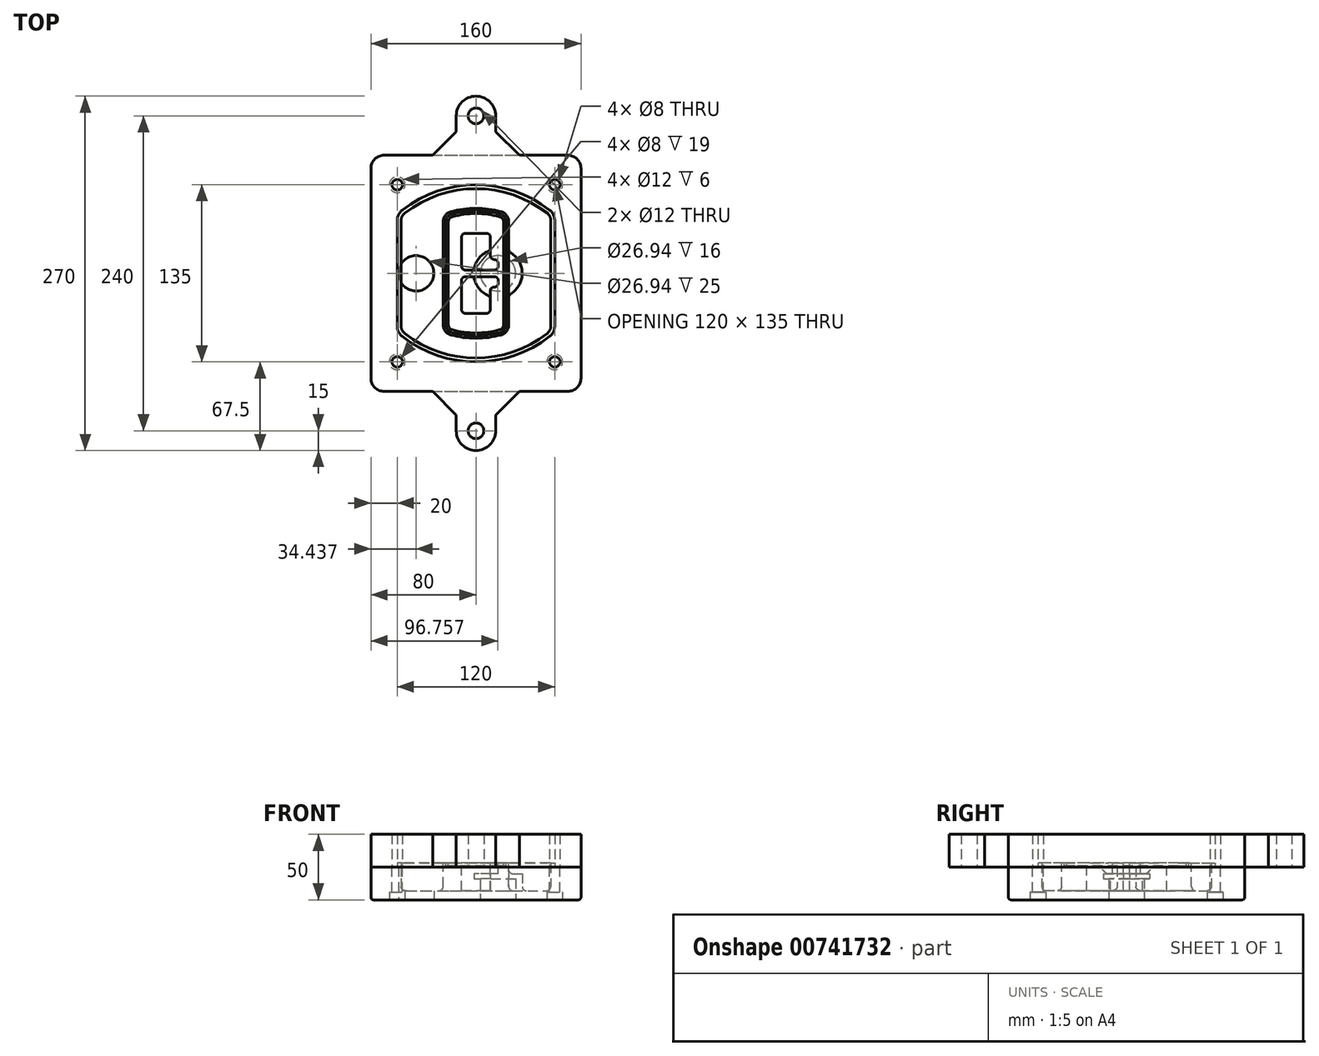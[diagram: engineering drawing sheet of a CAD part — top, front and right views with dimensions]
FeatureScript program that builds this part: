
annotation { "Feature Type Name" : "Feature", "Feature Type Description" : "" }
export const myFeature = defineFeature(function(context is Context, id is Id, definition is map)
    precondition{}
    {
        {
            var Q0;
            Q0=qCreatedBy(makeId("Top.planeOp"),FACE);
            var sketch = newSketch(context, id + "F0", { "sketchPlane" : qUnion([Q0])});
            skPoint(sketch, "E0.rect.middle", {"position": v(0, 0) * mm});
            skLineSegment(sketch, "E1.bottom", {"start": v(-70, -90) * mm, "end": v(70, -90) * mm});
            skLineSegment(sketch, "E1.top", {"start": v(-70, 90) * mm, "end": v(70, 90) * mm});
            skLineSegment(sketch, "E1.left", {"start": v(-80, -80) * mm, "end": v(-80, 80) * mm});
            skLineSegment(sketch, "E1.right", {"start": v(80, -80) * mm, "end": v(80, 80) * mm});
            skLineSegment(sketch, "E2", {"start": v(-80, 90) * mm, "end": v(80, -90) * mm, "construction": true});
            skLineSegment(sketch, "E3", {"start": v(80, 90) * mm, "end": v(-80, -90) * mm, "construction": true});
            skCircle(sketch, "E4", {"center": v(-60, 67.5) * mm, "radius": 4 * mm});
            skCircle(sketch, "E5", {"center": v(60, 67.5) * mm, "radius": 4 * mm});
            skCircle(sketch, "E6", {"center": v(60, -67.5) * mm, "radius": 4 * mm});
            skCircle(sketch, "E7", {"center": v(-60, -67.5) * mm, "radius": 4 * mm});
            skLineSegment(sketch, "E8", {"start": v(-60, 67.5) * mm, "end": v(60, 67.5) * mm, "construction": true});
            skLineSegment(sketch, "E9", {"start": v(60, 67.5) * mm, "end": v(60, -67.5) * mm, "construction": true});
            skLineSegment(sketch, "E10", {"start": v(60, -67.5) * mm, "end": v(-60, -67.5) * mm, "construction": true});
            skLineSegment(sketch, "E11", {"start": v(-60, -67.5) * mm, "end": v(-60, 67.5) * mm, "construction": true});
            skLineSegment(sketch, "E12", {"start": v(-60, 40.3) * mm, "end": v(-60, -40.3) * mm});
            skLineSegment(sketch, "E13", {"start": v(60, 40.3) * mm, "end": v(60, -40.3) * mm});
            skArc(sketch, "E14", {"start": v(56.15, 48.18) * mm, "mid": v(0, 67.5) * mm, "end": v(-56.15, 48.18) * mm});
            skArc(sketch, "E15", {"start": v(-56.15, -48.18) * mm, "mid": v(0, -67.5) * mm, "end": v(56.15, -48.18) * mm});
            skLineSegment(sketch, "E16", {"start": v(-60, 0) * mm, "end": v(60, 0) * mm, "construction": true});
            skPoint(sketch, "E17.visualSharp", {"position": v(-60, -45) * mm});
            skArc(sketch, "E17.filletArc", {"start": v(-60, -40.3) * mm, "mid": v(-58.99, -44.68) * mm, "end": v(-56.15, -48.18) * mm});
            skPoint(sketch, "E18.visualSharp", {"position": v(-60, 45) * mm});
            skArc(sketch, "E18.filletArc", {"start": v(-56.15, 48.18) * mm, "mid": v(-58.99, 44.68) * mm, "end": v(-60, 40.3) * mm});
            skPoint(sketch, "E19.visualSharp", {"position": v(60, 45) * mm});
            skArc(sketch, "E19.filletArc", {"start": v(60, 40.3) * mm, "mid": v(58.99, 44.68) * mm, "end": v(56.15, 48.18) * mm});
            skPoint(sketch, "E20.visualSharp", {"position": v(60, -45) * mm});
            skArc(sketch, "E20.filletArc", {"start": v(56.15, -48.18) * mm, "mid": v(58.99, -44.68) * mm, "end": v(60, -40.3) * mm});
            skPoint(sketch, "E21.visualSharp", {"position": v(-80, 90) * mm});
            skArc(sketch, "E21.filletArc", {"start": v(-70, 90) * mm, "mid": v(-77.07, 87.07) * mm, "end": v(-80, 80) * mm});
            skPoint(sketch, "E22.visualSharp", {"position": v(80, 90) * mm});
            skArc(sketch, "E22.filletArc", {"start": v(80, 80) * mm, "mid": v(77.07, 87.07) * mm, "end": v(70, 90) * mm});
            skPoint(sketch, "E23.visualSharp", {"position": v(80, -90) * mm});
            skArc(sketch, "E23.filletArc", {"start": v(70, -90) * mm, "mid": v(77.07, -87.07) * mm, "end": v(80, -80) * mm});
            skPoint(sketch, "E24.visualSharp", {"position": v(-80, -90) * mm});
            skArc(sketch, "E24.filletArc", {"start": v(-80, -80) * mm, "mid": v(-77.07, -87.07) * mm, "end": v(-70, -90) * mm});
            skArc(sketch, "E25.0", {"start": v(57, 40.3) * mm, "mid": v(56.3, 43.36) * mm, "end": v(54.3, 45.81) * mm});
            skLineSegment(sketch, "E25.1", {"start": v(57, 40.3) * mm, "end": v(57, -40.3) * mm});
            skArc(sketch, "E25.2", {"start": v(54.3, -45.81) * mm, "mid": v(56.3, -43.36) * mm, "end": v(57, -40.3) * mm});
            skArc(sketch, "E25.3", {"start": v(-54.3, -45.81) * mm, "mid": v(0, -64.5) * mm, "end": v(54.3, -45.81) * mm});
            skArc(sketch, "E25.4", {"start": v(-57, -40.3) * mm, "mid": v(-56.3, -43.36) * mm, "end": v(-54.3, -45.81) * mm});
            skArc(sketch, "E25.5", {"start": v(54.3, 45.81) * mm, "mid": v(0, 64.5) * mm, "end": v(-54.3, 45.81) * mm});
            skLineSegment(sketch, "E25.6", {"start": v(-57, 40.3) * mm, "end": v(-57, -40.3) * mm});
            skArc(sketch, "E25.7", {"start": v(-54.3, 45.81) * mm, "mid": v(-56.3, 43.36) * mm, "end": v(-57, 40.3) * mm});
            skArc(sketch, "E26.0", {"start": v(-58.62, 51.33) * mm, "mid": v(-62.58, 46.43) * mm, "end": v(-64, 40.3) * mm});
            skArc(sketch, "E26.1", {"start": v(58.62, 51.33) * mm, "mid": v(0, 71.5) * mm, "end": v(-58.62, 51.33) * mm});
            skArc(sketch, "E26.2", {"start": v(64, 40.3) * mm, "mid": v(62.58, 46.43) * mm, "end": v(58.62, 51.33) * mm});
            skLineSegment(sketch, "E26.3", {"start": v(64, 40.3) * mm, "end": v(64, -40.3) * mm});
            skArc(sketch, "E26.4", {"start": v(58.62, -51.33) * mm, "mid": v(62.58, -46.43) * mm, "end": v(64, -40.3) * mm});
            skLineSegment(sketch, "E26.5", {"start": v(-64, 40.3) * mm, "end": v(-64, -40.3) * mm});
            skArc(sketch, "E26.6", {"start": v(-58.62, -51.33) * mm, "mid": v(0, -71.5) * mm, "end": v(58.62, -51.33) * mm});
            skArc(sketch, "E26.7", {"start": v(-64, -40.3) * mm, "mid": v(-62.58, -46.43) * mm, "end": v(-58.62, -51.33) * mm});
            skSolve(sketch);
        }
        {
            var Q0;
            Q0=makeQuery(id+"F0.imprint","IMPRINT",FACE,{"disambiguationData":[TD([[makeQuery(id+"F0.imprint","IMPRINT",EDGE,{"derivedFrom":sQuery(id+"F0.wireOp",EDGE,"E1.bottom")}),1.0]])]});
            var Q1;
            Q1=makeQuery(id+"F0.imprint","IMPRINT",FACE,{"disambiguationData":[TD([[makeQuery(id+"F0.imprint","IMPRINT",EDGE,{"derivedFrom":sQuery(id+"F0.wireOp",EDGE,"E12")}),1.0]])]});
            var Q2;
            Q2=makeQuery(id+"F0.imprint","IMPRINT",FACE,{"disambiguationData":[TD([[makeQuery(id+"F0.imprint","IMPRINT",EDGE,{"derivedFrom":sQuery(id+"F0.wireOp",EDGE,"E25.0")}),1.0]])]});
            var Q3;
            Q3=makeQuery(id+"F0.imprint","IMPRINT",FACE,{"disambiguationData":[TD([[makeQuery(id+"F0.imprint","IMPRINT",EDGE,{"derivedFrom":sQuery(id+"F0.wireOp",EDGE,"E12")}),-1.0]])]});
            extrude(context, id + "F1", {"entities" : qUnion([Q0, Q1, Q2, Q3]), "oppositeDirection" : true, "depth" : 25 * mm});
        }
        {
            var Q0;
            Q0=makeQuery(id+"F0.imprint","IMPRINT",FACE,{"disambiguationData":[TD([[makeQuery(id+"F0.imprint","IMPRINT",EDGE,{"derivedFrom":sQuery(id+"F0.wireOp",EDGE,"E12")}),1.0]])]});
            extrude(context, id + "F2", {"entities" : qUnion([Q0]), "operationType" : NewBodyOperationType.ADD, "depth" : 3 * mm});
        }
        {
            var Q0;
            Q0=makeQuery(id+"F0.imprint","IMPRINT",FACE,{"disambiguationData":[TD([[makeQuery(id+"F0.imprint","IMPRINT",EDGE,{"derivedFrom":sQuery(id+"F0.wireOp",EDGE,"E25.0")}),1.0]])]});
            extrude(context, id + "F3", {"entities" : qUnion([Q0]), "operationType" : NewBodyOperationType.REMOVE, "oppositeDirection" : true, "depth" : 18 * mm});
        }
        {
            var Q0;
            Q0=makeQuery(id+"F2.opExtrude","CAP_FACE",FACE,{"disambiguationData":[OSD([sQuery(id+"F0.wireOp",EDGE,"E12"),sQuery(id+"F0.wireOp",EDGE,"E13"),sQuery(id+"F0.wireOp",EDGE,"E14"),sQuery(id+"F0.wireOp",EDGE,"E15"),sQuery(id+"F0.wireOp",EDGE,"E17.filletArc"),sQuery(id+"F0.wireOp",EDGE,"E18.filletArc"),sQuery(id+"F0.wireOp",EDGE,"E19.filletArc"),sQuery(id+"F0.wireOp",EDGE,"E20.filletArc"),sQuery(id+"F0.wireOp",EDGE,"E25.0"),sQuery(id+"F0.wireOp",EDGE,"E25.1"),sQuery(id+"F0.wireOp",EDGE,"E25.2"),sQuery(id+"F0.wireOp",EDGE,"E25.3"),sQuery(id+"F0.wireOp",EDGE,"E25.4"),sQuery(id+"F0.wireOp",EDGE,"E25.5"),sQuery(id+"F0.wireOp",EDGE,"E25.6"),sQuery(id+"F0.wireOp",EDGE,"E25.7")])],"isStart":false});
            var sketch = newSketch(context, id + "F4", { "sketchPlane" : qUnion([Q0])});
            skArc(sketch, "E27.0", {"start": v(-19.08, -46.97) * mm, "mid": v(0, -49.5) * mm, "end": v(19.08, -46.97) * mm});
            skArc(sketch, "E28.0", {"start": v(19.08, 46.97) * mm, "mid": v(0, 49.5) * mm, "end": v(-19.08, 46.97) * mm});
            skLineSegment(sketch, "E29", {"start": v(-25, 39.25) * mm, "end": v(-25, -39.25) * mm});
            skLineSegment(sketch, "E30", {"start": v(25, 39.25) * mm, "end": v(25, -39.25) * mm});
            skLineSegment(sketch, "E31", {"start": v(-25, 45.1) * mm, "end": v(25, 45.1) * mm, "construction": true});
            skLineSegment(sketch, "E32", {"start": v(-25, -45.1) * mm, "end": v(25, -45.1) * mm, "construction": true});
            skPoint(sketch, "E33.visualSharp", {"position": v(-25, 45.1) * mm});
            skArc(sketch, "E33.filletArc", {"start": v(-19.08, 46.97) * mm, "mid": v(-23.35, 44.11) * mm, "end": v(-25, 39.25) * mm});
            skPoint(sketch, "E34.visualSharp", {"position": v(25, 45.1) * mm});
            skArc(sketch, "E34.filletArc", {"start": v(25, 39.25) * mm, "mid": v(23.35, 44.11) * mm, "end": v(19.08, 46.97) * mm});
            skPoint(sketch, "E35.visualSharp", {"position": v(25, -45.1) * mm});
            skArc(sketch, "E35.filletArc", {"start": v(19.08, -46.97) * mm, "mid": v(23.35, -44.11) * mm, "end": v(25, -39.25) * mm});
            skPoint(sketch, "E36.visualSharp", {"position": v(-25, -45.1) * mm});
            skArc(sketch, "E36.filletArc", {"start": v(-25, -39.25) * mm, "mid": v(-23.35, -44.11) * mm, "end": v(-19.08, -46.97) * mm});
            skArc(sketch, "E37.0", {"start": v(54.3, 45.81) * mm, "mid": v(0, 64.5) * mm, "end": v(-54.3, 45.81) * mm});
            skArc(sketch, "E37.1", {"start": v(-54.3, 45.81) * mm, "mid": v(-56.3, 43.36) * mm, "end": v(-57, 40.3) * mm});
            skLineSegment(sketch, "E37.2", {"start": v(-57, 40.3) * mm, "end": v(-57, -40.3) * mm});
            skArc(sketch, "E37.3", {"start": v(-57, -40.3) * mm, "mid": v(-56.3, -43.36) * mm, "end": v(-54.3, -45.81) * mm});
            skArc(sketch, "E37.4", {"start": v(-54.3, -45.81) * mm, "mid": v(0, -64.5) * mm, "end": v(54.3, -45.81) * mm});
            skArc(sketch, "E37.5", {"start": v(54.3, -45.81) * mm, "mid": v(56.3, -43.36) * mm, "end": v(57, -40.3) * mm});
            skLineSegment(sketch, "E37.6", {"start": v(57, 40.3) * mm, "end": v(57, -40.3) * mm});
            skArc(sketch, "E37.7", {"start": v(57, 40.3) * mm, "mid": v(56.3, 43.36) * mm, "end": v(54.3, 45.81) * mm});
            skLineSegment(sketch, "E38.0", {"start": v(23, 39.25) * mm, "end": v(23, -39.25) * mm});
            skArc(sketch, "E38.1", {"start": v(18.56, -45.04) * mm, "mid": v(21.76, -42.9) * mm, "end": v(23, -39.25) * mm});
            skArc(sketch, "E38.2", {"start": v(-18.56, -45.04) * mm, "mid": v(0, -47.5) * mm, "end": v(18.56, -45.04) * mm});
            skArc(sketch, "E38.3", {"start": v(-23, -39.25) * mm, "mid": v(-21.76, -42.9) * mm, "end": v(-18.56, -45.04) * mm});
            skLineSegment(sketch, "E38.4", {"start": v(-23, 39.25) * mm, "end": v(-23, -39.25) * mm});
            skArc(sketch, "E38.5", {"start": v(23, 39.25) * mm, "mid": v(21.76, 42.9) * mm, "end": v(18.56, 45.04) * mm});
            skArc(sketch, "E38.6", {"start": v(-18.56, 45.04) * mm, "mid": v(-21.76, 42.9) * mm, "end": v(-23, 39.25) * mm});
            skArc(sketch, "E38.7", {"start": v(18.56, 45.04) * mm, "mid": v(0, 47.5) * mm, "end": v(-18.56, 45.04) * mm});
            skArc(sketch, "E39.0", {"start": v(21, 39.25) * mm, "mid": v(20.18, 41.68) * mm, "end": v(18.04, 43.1) * mm});
            skLineSegment(sketch, "E39.1", {"start": v(21, 39.25) * mm, "end": v(21, -39.25) * mm});
            skArc(sketch, "E39.2", {"start": v(18.04, -43.1) * mm, "mid": v(20.18, -41.68) * mm, "end": v(21, -39.25) * mm});
            skArc(sketch, "E39.3", {"start": v(-18.04, -43.1) * mm, "mid": v(0, -45.5) * mm, "end": v(18.04, -43.1) * mm});
            skArc(sketch, "E39.4", {"start": v(-21, -39.25) * mm, "mid": v(-20.18, -41.68) * mm, "end": v(-18.04, -43.1) * mm});
            skArc(sketch, "E39.5", {"start": v(18.04, 43.1) * mm, "mid": v(0, 45.5) * mm, "end": v(-18.04, 43.1) * mm});
            skLineSegment(sketch, "E39.6", {"start": v(-21, 39.25) * mm, "end": v(-21, -39.25) * mm});
            skArc(sketch, "E39.7", {"start": v(-18.04, 43.1) * mm, "mid": v(-20.18, 41.68) * mm, "end": v(-21, 39.25) * mm});
            skLineSegment(sketch, "E40", {"start": v(-25, 0) * mm, "end": v(25, 0) * mm, "construction": true});
            skLineSegment(sketch, "E41", {"start": v(-11, 5.5) * mm, "end": v(-11, 27.5) * mm});
            skLineSegment(sketch, "E42", {"start": v(-8, 30.5) * mm, "end": v(8, 30.5) * mm});
            skLineSegment(sketch, "E43", {"start": v(11, 27.5) * mm, "end": v(11, 13.5) * mm});
            skLineSegment(sketch, "E44", {"start": v(14, 10.5) * mm, "end": v(14, 10.5) * mm});
            skLineSegment(sketch, "E45", {"start": v(17, 7.5) * mm, "end": v(17, 5.5) * mm});
            skLineSegment(sketch, "E46", {"start": v(14, 2.5) * mm, "end": v(-8, 2.5) * mm});
            skPoint(sketch, "E47.visualSharp", {"position": v(-11, 30.5) * mm});
            skArc(sketch, "E47.filletArc", {"start": v(-8, 30.5) * mm, "mid": v(-10.12, 29.62) * mm, "end": v(-11, 27.5) * mm});
            skPoint(sketch, "E48.visualSharp", {"position": v(11, 30.5) * mm});
            skArc(sketch, "E48.filletArc", {"start": v(11, 27.5) * mm, "mid": v(10.12, 29.62) * mm, "end": v(8, 30.5) * mm});
            skPoint(sketch, "E49.visualSharp", {"position": v(11, 10.5) * mm});
            skArc(sketch, "E49.filletArc", {"start": v(11, 13.5) * mm, "mid": v(11.88, 11.38) * mm, "end": v(14, 10.5) * mm});
            skPoint(sketch, "E50.visualSharp", {"position": v(17, 10.5) * mm});
            skArc(sketch, "E50.filletArc", {"start": v(17, 7.5) * mm, "mid": v(16.12, 9.62) * mm, "end": v(14, 10.5) * mm});
            skPoint(sketch, "E51.visualSharp", {"position": v(17, 2.5) * mm});
            skArc(sketch, "E51.filletArc", {"start": v(14, 2.5) * mm, "mid": v(16.12, 3.38) * mm, "end": v(17, 5.5) * mm});
            skPoint(sketch, "E52.visualSharp", {"position": v(-11, 2.5) * mm});
            skArc(sketch, "E52.filletArc", {"start": v(-11, 5.5) * mm, "mid": v(-10.12, 3.38) * mm, "end": v(-8, 2.5) * mm});
            skLineSegment(sketch, "E53.0.MirrorCS", {"start": v(14, -2.5) * mm, "end": v(-8, -2.5) * mm});
            skArc(sketch, "E54.0.MirrorCS", {"start": v(-11, -5.5) * mm, "mid": v(-10.12, -3.38) * mm, "end": v(-8, -2.5) * mm});
            skLineSegment(sketch, "E55.0.MirrorCS", {"start": v(-11, -5.5) * mm, "end": v(-11, -27.5) * mm});
            skArc(sketch, "E56.0.MirrorCS", {"start": v(-8, -30.5) * mm, "mid": v(-10.12, -29.62) * mm, "end": v(-11, -27.5) * mm});
            skLineSegment(sketch, "E57.0.MirrorCS", {"start": v(-8, -30.5) * mm, "end": v(8, -30.5) * mm});
            skArc(sketch, "E58.0.MirrorCS", {"start": v(11, -27.5) * mm, "mid": v(10.12, -29.62) * mm, "end": v(8, -30.5) * mm});
            skLineSegment(sketch, "E59.0.MirrorCS", {"start": v(11, -27.5) * mm, "end": v(11, -13.5) * mm});
            skArc(sketch, "E60.0.MirrorCS", {"start": v(11, -13.5) * mm, "mid": v(11.88, -11.38) * mm, "end": v(14, -10.5) * mm});
            skArc(sketch, "E61.0.MirrorCS", {"start": v(17, -7.5) * mm, "mid": v(16.12, -9.62) * mm, "end": v(14, -10.5) * mm});
            skLineSegment(sketch, "E62.0.MirrorCS", {"start": v(17, -7.5) * mm, "end": v(17, -5.5) * mm});
            skArc(sketch, "E63.0.MirrorCS", {"start": v(14, -2.5) * mm, "mid": v(16.12, -3.38) * mm, "end": v(17, -5.5) * mm});
            skSolve(sketch);
        }
        {
            var Q0;
            Q0=makeQuery(id+"F4.imprint","IMPRINT",FACE,{"disambiguationData":[TD([[makeQuery(id+"F4.imprint","IMPRINT",EDGE,{"derivedFrom":sQuery(id+"F4.wireOp",EDGE,"E27.0")}),1.0]])]});
            var Q1;
            Q1=makeQuery(id+"F4.imprint","IMPRINT",FACE,{"disambiguationData":[TD([[makeQuery(id+"F4.imprint","IMPRINT",EDGE,{"derivedFrom":sQuery(id+"F4.wireOp",EDGE,"E38.0")}),-1.0]])]});
            var Q2;
            Q2=makeQuery(id+"F4.imprint","IMPRINT",FACE,{"disambiguationData":[TD([[makeQuery(id+"F4.imprint","IMPRINT",EDGE,{"derivedFrom":sQuery(id+"F4.wireOp",EDGE,"E39.0")}),1.0]])]});
            extrude(context, id + "F5", {"entities" : qUnion([Q0, Q1, Q2]), "operationType" : NewBodyOperationType.ADD, "endBound" : BoundingType.UP_TO_NEXT, "oppositeDirection" : true, "depth" : 25 * mm});
        }
        {
            var Q0;
            Q0=makeQuery(id+"F4.imprint","IMPRINT",FACE,{"disambiguationData":[TD([[makeQuery(id+"F4.imprint","IMPRINT",EDGE,{"derivedFrom":sQuery(id+"F4.wireOp",EDGE,"E38.0")}),-1.0]])]});
            extrude(context, id + "F6", {"entities" : qUnion([Q0]), "operationType" : NewBodyOperationType.REMOVE, "oppositeDirection" : true, "depth" : 2 * mm});
        }
        {
            var Q0;
            Q0=makeQuery(id+"F1.opExtrude","CAP_FACE",FACE,{"disambiguationData":[OSD([sQuery(id+"F0.wireOp",EDGE,"E1.bottom"),sQuery(id+"F0.wireOp",EDGE,"E1.top"),sQuery(id+"F0.wireOp",EDGE,"E1.left"),sQuery(id+"F0.wireOp",EDGE,"E1.right"),sQuery(id+"F0.wireOp",EDGE,"E4"),sQuery(id+"F0.wireOp",EDGE,"E5"),sQuery(id+"F0.wireOp",EDGE,"E6"),sQuery(id+"F0.wireOp",EDGE,"E7"),sQuery(id+"F0.wireOp",EDGE,"E21.filletArc"),sQuery(id+"F0.wireOp",EDGE,"E22.filletArc"),sQuery(id+"F0.wireOp",EDGE,"E23.filletArc"),sQuery(id+"F0.wireOp",EDGE,"E24.filletArc")])],"isStart":false});
            var sketch = newSketch(context, id + "F7", { "sketchPlane" : qUnion([Q0])});
            skCircle(sketch, "E64", {"center": v(16.76, 0) * mm, "radius": 13.47 * mm});
            skCircle(sketch, "E65", {"center": v(-45.56, 0) * mm, "radius": 13.47 * mm});
            skLineSegment(sketch, "E66", {"start": v(80, 0) * mm, "end": v(-80, 0) * mm});
            skCircle(sketch, "E67", {"center": v(16.76, 0) * mm, "radius": 18.47 * mm});
            skCircle(sketch, "E68", {"center": v(60, -67.5) * mm, "radius": 6 * mm});
            skCircle(sketch, "E69", {"center": v(-60, -67.5) * mm, "radius": 6 * mm});
            skCircle(sketch, "E70", {"center": v(-60, 67.5) * mm, "radius": 6 * mm});
            skCircle(sketch, "E71", {"center": v(60, 67.5) * mm, "radius": 6 * mm});
            skSolve(sketch);
        }
        {
            var Q0;
            {var subQ1=sQuery(id+"F7.wireOp",EDGE,"E66");var subQ4=sQuery(id+"F7.wireOp",EDGE,"E64");var subQ6=makeQuery(id+"F7.imprint","INTERSECT",VERTEX,{"disambiguationData":[OD(0.0)],"derivedFrom":[subQ4,subQ1]});Q0=makeQuery(id+"F7.imprint","IMPRINT",FACE,{"disambiguationData":[TD([[makeQuery(id+"F7.imprint","IMPRINT",EDGE,{"disambiguationData":[TD([[subQ6,-1.0]])],"derivedFrom":subQ4}),-1.0]])]});}
            var Q1;
            {var subQ0=sQuery(id+"F7.wireOp",EDGE,"E66");var subQ1=sQuery(id+"F7.wireOp",EDGE,"E64");var subQ3=makeQuery(id+"F7.imprint","INTERSECT",VERTEX,{"disambiguationData":[OD(0.0)],"derivedFrom":[subQ1,subQ0]});Q1=makeQuery(id+"F7.imprint","IMPRINT",FACE,{"disambiguationData":[TD([[makeQuery(id+"F7.imprint","IMPRINT",EDGE,{"disambiguationData":[TD([[subQ3,-1.0]])],"derivedFrom":subQ1}),1.0]])]});}
            var Q2;
            {var subQ0=sQuery(id+"F7.wireOp",EDGE,"E66");var subQ1=sQuery(id+"F7.wireOp",EDGE,"E64");var subQ3=makeQuery(id+"F7.imprint","INTERSECT",VERTEX,{"disambiguationData":[OD(0.0)],"derivedFrom":[subQ1,subQ0]});Q2=makeQuery(id+"F7.imprint","IMPRINT",FACE,{"disambiguationData":[TD([[makeQuery(id+"F7.imprint","IMPRINT",EDGE,{"disambiguationData":[TD([[subQ3,1.0]])],"derivedFrom":subQ1}),1.0]])]});}
            var Q3;
            {var subQ1=sQuery(id+"F7.wireOp",EDGE,"E66");var subQ4=sQuery(id+"F7.wireOp",EDGE,"E64");var subQ6=makeQuery(id+"F7.imprint","INTERSECT",VERTEX,{"disambiguationData":[OD(0.0)],"derivedFrom":[subQ4,subQ1]});Q3=makeQuery(id+"F7.imprint","IMPRINT",FACE,{"disambiguationData":[TD([[makeQuery(id+"F7.imprint","IMPRINT",EDGE,{"disambiguationData":[TD([[subQ6,1.0]])],"derivedFrom":subQ4}),-1.0]])]});}
            extrude(context, id + "F8", {"entities" : qUnion([Q0, Q1, Q2, Q3]), "operationType" : NewBodyOperationType.ADD, "oppositeDirection" : true, "depth" : 20 * mm});
        }
        {
            var Q0;
            {var subQ0=sQuery(id+"F7.wireOp",EDGE,"E66");var subQ1=sQuery(id+"F7.wireOp",EDGE,"E64");var subQ3=makeQuery(id+"F7.imprint","INTERSECT",VERTEX,{"disambiguationData":[OD(0.0)],"derivedFrom":[subQ1,subQ0]});Q0=makeQuery(id+"F7.imprint","IMPRINT",FACE,{"disambiguationData":[TD([[makeQuery(id+"F7.imprint","IMPRINT",EDGE,{"disambiguationData":[TD([[subQ3,-1.0]])],"derivedFrom":subQ1}),1.0]])]});}
            var Q1;
            {var subQ0=sQuery(id+"F7.wireOp",EDGE,"E66");var subQ1=sQuery(id+"F7.wireOp",EDGE,"E64");var subQ3=makeQuery(id+"F7.imprint","INTERSECT",VERTEX,{"disambiguationData":[OD(0.0)],"derivedFrom":[subQ1,subQ0]});Q1=makeQuery(id+"F7.imprint","IMPRINT",FACE,{"disambiguationData":[TD([[makeQuery(id+"F7.imprint","IMPRINT",EDGE,{"disambiguationData":[TD([[subQ3,1.0]])],"derivedFrom":subQ1}),1.0]])]});}
            extrude(context, id + "F9", {"entities" : qUnion([Q0, Q1]), "operationType" : NewBodyOperationType.REMOVE, "oppositeDirection" : true, "depth" : 16 * mm});
        }
        {
            var Q0;
            {var subQ0=sQuery(id+"F7.wireOp",EDGE,"E66");var subQ1=sQuery(id+"F7.wireOp",EDGE,"E65");var subQ3=makeQuery(id+"F7.imprint","INTERSECT",VERTEX,{"disambiguationData":[OD(0.0)],"derivedFrom":[subQ1,subQ0]});Q0=makeQuery(id+"F7.imprint","IMPRINT",FACE,{"disambiguationData":[TD([[makeQuery(id+"F7.imprint","IMPRINT",EDGE,{"disambiguationData":[TD([[subQ3,-1.0]])],"derivedFrom":subQ1}),1.0]])]});}
            var Q1;
            {var subQ0=sQuery(id+"F7.wireOp",EDGE,"E66");var subQ1=sQuery(id+"F7.wireOp",EDGE,"E65");var subQ3=makeQuery(id+"F7.imprint","INTERSECT",VERTEX,{"disambiguationData":[OD(0.0)],"derivedFrom":[subQ1,subQ0]});Q1=makeQuery(id+"F7.imprint","IMPRINT",FACE,{"disambiguationData":[TD([[makeQuery(id+"F7.imprint","IMPRINT",EDGE,{"disambiguationData":[TD([[subQ3,1.0]])],"derivedFrom":subQ1}),1.0]])]});}
            extrude(context, id + "F10", {"entities" : qUnion([Q0, Q1]), "operationType" : NewBodyOperationType.REMOVE, "oppositeDirection" : true, "depth" : 25 * mm});
        }
        {
            var Q0;
            Q0=makeQuery(id+"F7.imprint","IMPRINT",FACE,{"disambiguationData":[TD([[makeQuery(id+"F7.imprint","IMPRINT",EDGE,{"derivedFrom":sQuery(id+"F7.wireOp",EDGE,"E68")}),1.0]])]});
            var Q1;
            Q1=makeQuery(id+"F7.imprint","IMPRINT",FACE,{"disambiguationData":[TD([[makeQuery(id+"F7.imprint","IMPRINT",EDGE,{"derivedFrom":makeQuery(id+"F1.opExtrude","CAP_EDGE",EDGE,{"disambiguationData":[OSD([sQuery(id+"F0.wireOp",EDGE,"E5")])],"isStart":false})}),-1.0]])]});
            var Q2;
            Q2=makeQuery(id+"F7.imprint","IMPRINT",FACE,{"disambiguationData":[TD([[makeQuery(id+"F7.imprint","IMPRINT",EDGE,{"derivedFrom":sQuery(id+"F7.wireOp",EDGE,"E69")}),1.0]])]});
            var Q3;
            Q3=makeQuery(id+"F7.imprint","IMPRINT",FACE,{"disambiguationData":[TD([[makeQuery(id+"F7.imprint","IMPRINT",EDGE,{"derivedFrom":makeQuery(id+"F1.opExtrude","CAP_EDGE",EDGE,{"disambiguationData":[OSD([sQuery(id+"F0.wireOp",EDGE,"E4")])],"isStart":false})}),-1.0]])]});
            var Q4;
            Q4=makeQuery(id+"F7.imprint","IMPRINT",FACE,{"disambiguationData":[TD([[makeQuery(id+"F7.imprint","IMPRINT",EDGE,{"derivedFrom":sQuery(id+"F7.wireOp",EDGE,"E70")}),1.0]])]});
            var Q5;
            Q5=makeQuery(id+"F7.imprint","IMPRINT",FACE,{"disambiguationData":[TD([[makeQuery(id+"F7.imprint","IMPRINT",EDGE,{"derivedFrom":makeQuery(id+"F1.opExtrude","CAP_EDGE",EDGE,{"disambiguationData":[OSD([sQuery(id+"F0.wireOp",EDGE,"E7")])],"isStart":false})}),-1.0]])]});
            var Q6;
            Q6=makeQuery(id+"F7.imprint","IMPRINT",FACE,{"disambiguationData":[TD([[makeQuery(id+"F7.imprint","IMPRINT",EDGE,{"derivedFrom":sQuery(id+"F7.wireOp",EDGE,"E71")}),1.0]])]});
            var Q7;
            Q7=makeQuery(id+"F7.imprint","IMPRINT",FACE,{"disambiguationData":[TD([[makeQuery(id+"F7.imprint","IMPRINT",EDGE,{"derivedFrom":makeQuery(id+"F1.opExtrude","CAP_EDGE",EDGE,{"disambiguationData":[OSD([sQuery(id+"F0.wireOp",EDGE,"E6")])],"isStart":false})}),-1.0]])]});
            extrude(context, id + "F11", {"entities" : qUnion([Q0, Q1, Q2, Q3, Q4, Q5, Q6, Q7]), "operationType" : NewBodyOperationType.REMOVE, "oppositeDirection" : true, "depth" : 6 * mm});
        }
        {
            var Q0;
            Q0=makeQuery(id+"F9.boolean.opBoolean","COPY",FACE,{"derivedFrom":makeQuery(id+"F9.opExtrude","CAP_FACE",FACE,{"disambiguationData":[OSD([sQuery(id+"F7.wireOp",EDGE,"E64")])],"isStart":false})});
            var sketch = newSketch(context, id + "F12", { "sketchPlane" : qUnion([Q0])});
            skArc(sketch, "E72.0", {"start": v(11, 17.55) * mm, "mid": v(2.57, 11.82) * mm, "end": v(-1.54, 2.5) * mm});
            skArc(sketch, "E72.1", {"start": v(-1.54, -2.5) * mm, "mid": v(2.57, -11.82) * mm, "end": v(11, -17.55) * mm});
            skLineSegment(sketch, "E73", {"start": v(-1.54, -2.5) * mm, "end": v(14, -2.5) * mm});
            skLineSegment(sketch, "E74.0", {"start": v(14, 2.5) * mm, "end": v(-1.54, 2.5) * mm});
            skArc(sketch, "E74.1", {"start": v(14, 2.5) * mm, "mid": v(16.12, 3.38) * mm, "end": v(17, 5.5) * mm});
            skLineSegment(sketch, "E74.2", {"start": v(17, 7.5) * mm, "end": v(17, 5.5) * mm});
            skArc(sketch, "E74.3", {"start": v(17, 7.5) * mm, "mid": v(16.12, 9.62) * mm, "end": v(14, 10.5) * mm});
            skArc(sketch, "E74.4", {"start": v(11, 13.5) * mm, "mid": v(11.88, 11.38) * mm, "end": v(14, 10.5) * mm});
            skLineSegment(sketch, "E74.5", {"start": v(11, 17.55) * mm, "end": v(11, 13.5) * mm});
            skLineSegment(sketch, "E74.7", {"start": v(14, -2.5) * mm, "end": v(-1.54, -2.5) * mm});
            skArc(sketch, "E74.8", {"start": v(14, -2.5) * mm, "mid": v(16.12, -3.38) * mm, "end": v(17, -5.5) * mm});
            skLineSegment(sketch, "E74.9", {"start": v(17, -7.5) * mm, "end": v(17, -5.5) * mm});
            skArc(sketch, "E74.10", {"start": v(17, -7.5) * mm, "mid": v(16.12, -9.62) * mm, "end": v(14, -10.5) * mm});
            skArc(sketch, "E74.11", {"start": v(11, -13.5) * mm, "mid": v(11.88, -11.38) * mm, "end": v(14, -10.5) * mm});
            skLineSegment(sketch, "E74.12", {"start": v(11, -17.55) * mm, "end": v(11, -13.5) * mm});
            skPoint(sketch, "E75.orphan", {"position": v(11, -27.5) * mm});
            skPoint(sketch, "E76.orphan", {"position": v(-8, -2.5) * mm});
            skPoint(sketch, "E77.orphan", {"position": v(-8, 2.5) * mm});
            skPoint(sketch, "E78.orphan", {"position": v(11, 27.5) * mm});
            skSolve(sketch);
        }
        {
            var Q0;
            {var subQ7=sQuery(id+"F12.wireOp",EDGE,"E72.0");var subQ14=sQuery(id+"F12.wireOp",EDGE,"E72.1");var subQ16=sQuery(id+"F12.wireOp",EDGE,"E74.1");var subQ18=sQuery(id+"F12.wireOp",EDGE,"E74.8");Q0=qUnion([makeQuery(id+"F12.imprint","IMPRINT",FACE,{"disambiguationData":[TD([[makeQuery(id+"F12.imprint","IMPRINT",EDGE,{"derivedFrom":subQ7}),1.0]])]}),makeQuery(id+"F12.imprint","IMPRINT",FACE,{"disambiguationData":[TD([[makeQuery(id+"F12.imprint","IMPRINT",EDGE,{"derivedFrom":subQ14}),1.0]])]}),makeQuery(id+"F12.imprint","IMPRINT",FACE,{"disambiguationData":[TD([[makeQuery(id+"F12.imprint","IMPRINT",EDGE,{"derivedFrom":subQ16}),1.0]])]}),makeQuery(id+"F12.imprint","IMPRINT",FACE,{"disambiguationData":[TD([[makeQuery(id+"F12.imprint","IMPRINT",EDGE,{"derivedFrom":subQ18}),-1.0]])]})]);}
            var Q1;
            Q1=makeQuery(id+"F5.boolean.opBoolean","SPLIT",FACE,{"disambiguationData":[TD([makeQuery(id+"F5.opExtrude","SWEPT_FACE",FACE,{"disambiguationData":[OSD([sQuery(id+"F4.wireOp",EDGE,"E41")])]})])],"derivedFrom":makeQuery(id+"F3.boolean.opBoolean","COPY",FACE,{"derivedFrom":makeQuery(id+"F3.opExtrude","CAP_FACE",FACE,{"disambiguationData":[OSD([sQuery(id+"F0.wireOp",EDGE,"E25.0"),sQuery(id+"F0.wireOp",EDGE,"E25.1"),sQuery(id+"F0.wireOp",EDGE,"E25.2"),sQuery(id+"F0.wireOp",EDGE,"E25.3"),sQuery(id+"F0.wireOp",EDGE,"E25.4"),sQuery(id+"F0.wireOp",EDGE,"E25.5"),sQuery(id+"F0.wireOp",EDGE,"E25.6"),sQuery(id+"F0.wireOp",EDGE,"E25.7")])],"isStart":false})})});
            extrude(context, id + "F13", {"entities" : qUnion([Q0]), "operationType" : NewBodyOperationType.REMOVE, "endBound" : BoundingType.UP_TO_SURFACE, "endBoundEntityFace" : qUnion([Q1]), "depth" : 25 * mm});
        }
        {
            var Q0;
            Q0=makeQuery(id+"F3.boolean.opBoolean","COPY",EDGE,{"derivedFrom":makeQuery(id+"F3.opExtrude","CAP_EDGE",EDGE,{"disambiguationData":[OSD([sQuery(id+"F0.wireOp",EDGE,"E25.6")])],"isStart":false})});
            var Q1;
            Q1=makeQuery(id+"F8.boolean.opBoolean","INTERSECT",EDGE,{"derivedFrom":[makeQuery(id+"F5.opExtrude","SWEPT_FACE",FACE,{"disambiguationData":[OSD([sQuery(id+"F4.wireOp",EDGE,"E30")])]}),makeQuery(id+"F8.opExtrude","CAP_FACE",FACE,{"disambiguationData":[OSD([sQuery(id+"F7.wireOp",EDGE,"E67")])],"isStart":false})]});
            var Q2;
            Q2=makeQuery(id+"F8.boolean.opBoolean","INTERSECT",EDGE,{"disambiguationData":[OD(1.0)],"derivedFrom":[makeQuery(id+"F5.opExtrude","SWEPT_FACE",FACE,{"disambiguationData":[OSD([sQuery(id+"F4.wireOp",EDGE,"E30")])]}),makeQuery(id+"F8.opExtrude","SWEPT_FACE",FACE,{"disambiguationData":[OSD([sQuery(id+"F7.wireOp",EDGE,"E67")])]})]});
            var Q3;
            {var subQ0=sQuery(id+"F4.wireOp",EDGE,"E30");Q3=makeQuery(id+"F8.boolean.opBoolean","SPLIT",EDGE,{"disambiguationData":[TD([makeQuery(id+"F5.opExtrude","SWEPT_FACE",FACE,{"disambiguationData":[OSD([sQuery(id+"F4.wireOp",EDGE,"E35.filletArc")])]})])],"derivedFrom":makeQuery(id+"F5.opExtrude","CAP_EDGE",EDGE,{"disambiguationData":[OSD([subQ0])],"isStart":false})});}
            var Q4;
            {var subQ0=sQuery(id+"F0.wireOp",EDGE,"E25.7");var subQ1=sQuery(id+"F0.wireOp",EDGE,"E25.1");var subQ2=sQuery(id+"F0.wireOp",EDGE,"E25.6");var subQ3=sQuery(id+"F0.wireOp",EDGE,"E25.5");var subQ4=sQuery(id+"F0.wireOp",EDGE,"E25.4");var subQ5=sQuery(id+"F0.wireOp",EDGE,"E25.0");var subQ6=sQuery(id+"F0.wireOp",EDGE,"E25.2");var subQ7=sQuery(id+"F0.wireOp",EDGE,"E25.3");Q4=makeQuery(id+"F8.boolean.opBoolean","INTERSECT",EDGE,{"derivedFrom":[makeQuery(id+"F5.boolean.opBoolean","SPLIT",FACE,{"disambiguationData":[TD([makeQuery(id+"F2.opExtrude","SWEPT_FACE",FACE,{"disambiguationData":[OSD([subQ5])]})])],"derivedFrom":makeQuery(id+"F3.boolean.opBoolean","COPY",FACE,{"derivedFrom":makeQuery(id+"F3.opExtrude","CAP_FACE",FACE,{"disambiguationData":[OSD([subQ5,subQ1,subQ6,subQ7,subQ4,subQ3,subQ2,subQ0])],"isStart":false})})}),makeQuery(id+"F8.opExtrude","SWEPT_FACE",FACE,{"disambiguationData":[OSD([sQuery(id+"F7.wireOp",EDGE,"E67")])]})]});}
            var Q5;
            Q5=makeQuery(id+"F8.boolean.opBoolean","INTERSECT",EDGE,{"disambiguationData":[OD(0.0)],"derivedFrom":[makeQuery(id+"F5.opExtrude","SWEPT_FACE",FACE,{"disambiguationData":[OSD([sQuery(id+"F4.wireOp",EDGE,"E30")])]}),makeQuery(id+"F8.opExtrude","SWEPT_FACE",FACE,{"disambiguationData":[OSD([sQuery(id+"F7.wireOp",EDGE,"E67")])]})]});
            fillet(context, id + "F14", {"entities" : qUnion([Q0, Q1, Q2, Q3, Q4, Q5]), "radius" : 3 * mm, "tangentPropagation" : true, "allowEdgeOverflow" : false});
        }
        {
            var Q0;
            Q0=makeQuery(id+"F1.opExtrude","CAP_EDGE",EDGE,{"disambiguationData":[OSD([sQuery(id+"F0.wireOp",EDGE,"E1.bottom")])],"isStart":false});
            fillet(context, id + "F15", {"entities" : qUnion([Q0]), "radius" : 2 * mm, "tangentPropagation" : true, "allowEdgeOverflow" : false});
        }
        {
            var Q0;
            {var subQ0=sQuery(id+"F0.wireOp",EDGE,"E21.filletArc");var subQ1=sQuery(id+"F0.wireOp",EDGE,"E7");var subQ2=sQuery(id+"F0.wireOp",EDGE,"E6");var subQ3=sQuery(id+"F0.wireOp",EDGE,"E5");var subQ4=sQuery(id+"F0.wireOp",EDGE,"E4");var subQ5=sQuery(id+"F0.wireOp",EDGE,"E22.filletArc");var subQ6=sQuery(id+"F0.wireOp",EDGE,"E1.bottom");var subQ7=sQuery(id+"F0.wireOp",EDGE,"E1.right");var subQ8=sQuery(id+"F0.wireOp",EDGE,"E1.top");var subQ9=sQuery(id+"F0.wireOp",EDGE,"E1.left");var subQ10=sQuery(id+"F0.wireOp",EDGE,"E23.filletArc");var subQ11=sQuery(id+"F0.wireOp",EDGE,"E24.filletArc");Q0=makeQuery(id+"F2.boolean.opBoolean","SPLIT",FACE,{"disambiguationData":[TD([makeQuery(id+"F1.opExtrude","SWEPT_FACE",FACE,{"disambiguationData":[OSD([subQ6])]})])],"derivedFrom":makeQuery(id+"F1.opExtrude","CAP_FACE",FACE,{"disambiguationData":[OSD([subQ6,subQ8,subQ9,subQ7,subQ4,subQ3,subQ2,subQ1,subQ0,subQ5,subQ10,subQ11])],"isStart":true})});}
            var sketch = newSketch(context, id + "F16", { "sketchPlane" : qUnion([Q0])});
            skLineSegment(sketch, "E79", {"start": v(0, 90) * mm, "end": v(0, 120) * mm, "construction": true});
            skCircle(sketch, "E80", {"center": v(0, 120) * mm, "radius": 6 * mm});
            skLineSegment(sketch, "E81", {"start": v(-33, 90) * mm, "end": v(-15, 108) * mm});
            skLineSegment(sketch, "E82", {"start": v(-15, 108) * mm, "end": v(-15, 120) * mm});
            skLineSegment(sketch, "E83", {"start": v(33, 90) * mm, "end": v(15, 108) * mm});
            skLineSegment(sketch, "E84", {"start": v(15, 108) * mm, "end": v(15, 120) * mm});
            skArc(sketch, "E85", {"start": v(15, 120) * mm, "mid": v(0, 135) * mm, "end": v(-15, 120) * mm});
            skLineSegment(sketch, "E86", {"start": v(-80, 0) * mm, "end": v(80, 0) * mm, "construction": true});
            skLineSegment(sketch, "E87.MirrorCS", {"start": v(-33, -90) * mm, "end": v(-15, -108) * mm});
            skLineSegment(sketch, "E88.MirrorCS", {"start": v(-15, -108) * mm, "end": v(-15, -120) * mm});
            skArc(sketch, "E89.MirrorCS", {"start": v(15, -120) * mm, "mid": v(0, -135) * mm, "end": v(-15, -120) * mm});
            skLineSegment(sketch, "E90.MirrorCS", {"start": v(0, -90) * mm, "end": v(0, -120) * mm, "construction": true});
            skLineSegment(sketch, "E91.MirrorCS", {"start": v(33, -90) * mm, "end": v(15, -108) * mm});
            skLineSegment(sketch, "E92.MirrorCS", {"start": v(15, -108) * mm, "end": v(15, -120) * mm});
            skCircle(sketch, "E93.MirrorC", {"center": v(0, -120) * mm, "radius": 6 * mm});
            skSolve(sketch);
        }
        {
            var Q0;
            Q0=makeQuery(id+"F16.imprint","IMPRINT",FACE,{"disambiguationData":[TD([[makeQuery(id+"F16.imprint","IMPRINT",EDGE,{"derivedFrom":sQuery(id+"F16.wireOp",EDGE,"E80")}),-1.0]])]});
            var Q1;
            Q1=makeQuery(id+"F16.imprint","IMPRINT",FACE,{"disambiguationData":[TD([[makeQuery(id+"F16.imprint","IMPRINT",EDGE,{"derivedFrom":makeQuery(id+"F1.opExtrude","CAP_EDGE",EDGE,{"disambiguationData":[OSD([sQuery(id+"F0.wireOp",EDGE,"E1.left")])],"isStart":true})}),-1.0]])]});
            var Q2;
            {var subQ1=sQuery(id+"F16.wireOp",EDGE,"E87.MirrorCS");Q2=makeQuery(id+"F16.imprint","IMPRINT",FACE,{"disambiguationData":[TD([[makeQuery(id+"F16.imprint","IMPRINT",EDGE,{"derivedFrom":subQ1}),1.0]])]});}
            extrude(context, id + "F17", {"entities" : qUnion([Q0, Q1, Q2]), "depth" : 25 * mm, "offsetDistance" : 25 * mm});
        }
    });
